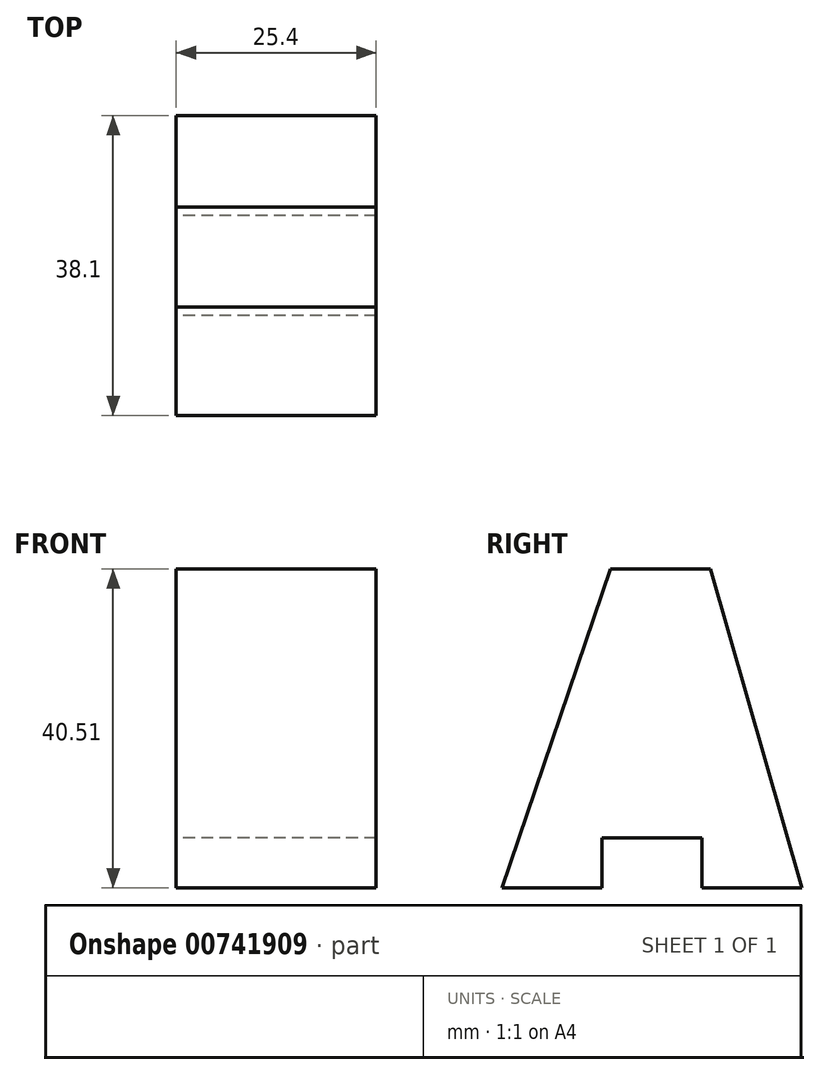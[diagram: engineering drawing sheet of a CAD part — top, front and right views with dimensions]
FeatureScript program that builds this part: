
annotation { "Feature Type Name" : "Feature", "Feature Type Description" : "" }
export const myFeature = defineFeature(function(context is Context, id is Id, definition is map)
    precondition{}
    {
        {
            var Q0;
            Q0=qCreatedBy(makeId("Right.planeOp"),FACE);
            var sketch = newSketch(context, id + "F0", { "sketchPlane" : qUnion([Q0])});
            skLineSegment(sketch, "E0", {"start": v(0, 0) * mm, "end": v(13.8, 40.5) * mm});
            skLineSegment(sketch, "E1", {"start": v(13.8, 40.5) * mm, "end": v(26.5, 40.5) * mm});
            skLineSegment(sketch, "E2", {"start": v(26.5, 40.5) * mm, "end": v(38.1, 0) * mm});
            skLineSegment(sketch, "E3", {"start": v(38.1, 0) * mm, "end": v(25.4, 0) * mm});
            skLineSegment(sketch, "E4", {"start": v(25.4, 0) * mm, "end": v(25.4, 6.35) * mm});
            skLineSegment(sketch, "E5", {"start": v(25.4, 6.35) * mm, "end": v(12.7, 6.35) * mm});
            skLineSegment(sketch, "E6", {"start": v(12.7, 6.35) * mm, "end": v(12.7, 0) * mm});
            skLineSegment(sketch, "E7", {"start": v(12.7, 0) * mm, "end": v(0, 0) * mm});
            skSolve(sketch);
        }
        {
            var Q0;
            Q0=makeQuery(id+"F0.imprint","IMPRINT",FACE,{"disambiguationData":[TD([[makeQuery(id+"F0.imprint","IMPRINT",EDGE,{"derivedFrom":sQuery(id+"F0.wireOp",EDGE,"E0")}),-1.0]])]});
            extrude(context, id + "F1", {"entities" : qUnion([Q0]), "depth" : 25.4 * mm, "offsetDistance" : 25.4 * mm});
        }
    });
